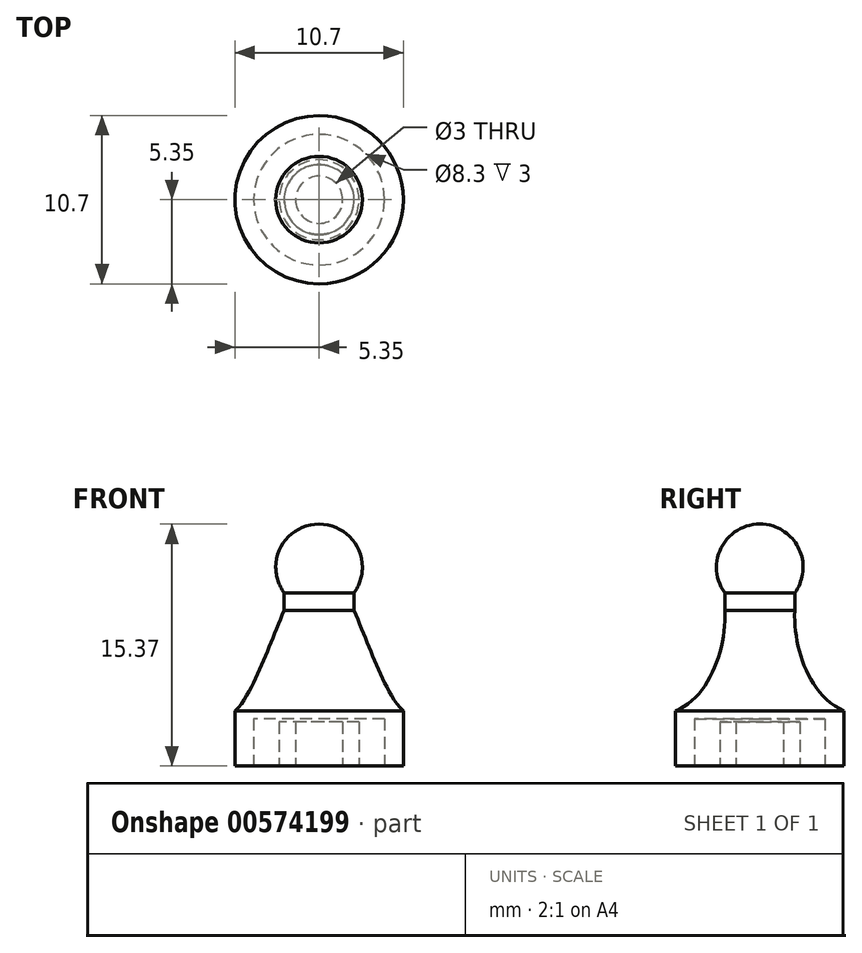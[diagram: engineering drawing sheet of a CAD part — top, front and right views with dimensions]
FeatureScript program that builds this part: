
annotation { "Feature Type Name" : "Feature", "Feature Type Description" : "" }
export const myFeature = defineFeature(function(context is Context, id is Id, definition is map)
    precondition{}
    {
        {
            var Q0;
            Q0=qCreatedBy(makeId("Top.planeOp"),FACE);
            var sketch = newSketch(context, id + "F0", { "sketchPlane" : qUnion([Q0])});
            skCircle(sketch, "E0", {"center": v(0, 0) * mm, "radius": 5.34 * mm});
            skPoint(sketch, "E1", {"position": v(0, -5.34) * mm});
            skSolve(sketch);
        }
        {
            var Q0;
            Q0=qCreatedBy(makeId("Top.planeOp"),FACE);
            cPlane(context, id + "F1", {"entities" : qUnion([Q0]), "cplaneType" : CPlaneType.OFFSET, "offset" : 9.87 * mm, "width" : 150 * mm, "height" : 150 * mm});
        }
        {
            var Q0;
            Q0=qCreatedBy(id+"F1.planeOp",FACE);
            var sketch = newSketch(context, id + "F2", { "sketchPlane" : qUnion([Q0])});
            skPoint(sketch, "E2", {"position": v(0, 0) * mm});
            skCircle(sketch, "E3", {"center": v(0, 0) * mm, "radius": 2.22 * mm});
            skPoint(sketch, "E4", {"position": v(0, -2.22) * mm});
            skSolve(sketch);
        }
        {
            var Q0;
            Q0=makeQuery(id+"F0.imprint","IMPRINT",FACE,{"disambiguationData":[TD([[makeQuery(id+"F0.imprint","IMPRINT",EDGE,{"derivedFrom":sQuery(id+"F0.wireOp",EDGE,"E0")}),1.0]])]});
            extrude(context, id + "F3", {"entities" : qUnion([Q0]), "depth" : 3.5 * mm, "offsetDistance" : 25 * mm});
        }
        {
            var Q0;
            Q0=qCreatedBy(makeId("Right.planeOp"),FACE);
            var sketch = newSketch(context, id + "F4", { "sketchPlane" : qUnion([Q0])});
            skPoint(sketch, "E5", {"position": v(-5.34, 3.5) * mm});
            skFitSpline(sketch, "E6", {"points": [v(-5.34, 3.5) * mm, v(-2.22, 9.87) * mm], "startDerivative": vector(6.48, 2.72) * mm, "endDerivative": vector(-0.3, 7.3) * mm});
            skLineSegment(sketch, "E7", {"start": v(0, 10.7) * mm, "end": v(0, 0) * mm, "construction": true});
            skFitSpline(sketch, "E8.MirrorCS", {"points": [v(5.35, 3.5) * mm, v(2.22, 9.87) * mm], "startDerivative": vector(-6.48, 2.72) * mm, "endDerivative": vector(0.3, 7.3) * mm});
            skSolve(sketch);
        }
        {
            var Q1;
            Q1=makeQuery(id+"F3.opExtrude","CAP_FACE",FACE,{"disambiguationData":[OSD([sQuery(id+"F0.wireOp",EDGE,"E0")])],"isStart":false});
            var Q2;
            Q2=makeQuery(id+"F2.imprint","IMPRINT",FACE,{"disambiguationData":[TD([[makeQuery(id+"F2.imprint","IMPRINT",EDGE,{"derivedFrom":sQuery(id+"F2.wireOp",EDGE,"E3")}),1.0]])]});
            var Q3;
            Q3=sQuery(id+"F4.wireOp",EDGE,"E6");
            var Q4;
            Q4=sQuery(id+"F4.wireOp",EDGE,"E8.MirrorCS");
            loft(context, id + "F5", {"operationType" : NewBodyOperationType.ADD, "addGuides" : true, "sheetProfilesArray" : [{ "sheetProfileEntities" : qUnion([Q1]) }, { "sheetProfileEntities" : qUnion([Q2]) }], "guidesArray" : [{ "guideEntities" : qUnion([Q3]), "guideDerivativeType" : LoftGuideDerivativeType.DEFAULT, "guideDerivativeMagnitude" : 1 }, { "guideEntities" : qUnion([Q4]), "guideDerivativeType" : LoftGuideDerivativeType.DEFAULT, "guideDerivativeMagnitude" : 1 }]});
        }
        {
            var Q0;
            Q0=qCreatedBy(id+"F1.planeOp",FACE);
            cPlane(context, id + "F6", {"entities" : qUnion([Q0]), "cplaneType" : CPlaneType.OFFSET, "offset" : (5.5 / 2) * mm, "width" : 150 * mm, "height" : 150 * mm});
        }
        {
            var Q0;
            Q0=qCreatedBy(id+"F6.planeOp",FACE);
            var sketch = newSketch(context, id + "F7", { "sketchPlane" : qUnion([Q0])});
            skPoint(sketch, "E9", {"position": v(0, 0) * mm});
            skArc(sketch, "E10", {"start": v(2.75, 0) * mm, "mid": v(0, 2.75) * mm, "end": v(-2.75, 0) * mm});
            skLineSegment(sketch, "E11", {"start": v(7.18, 0) * mm, "end": v(-9.15, 0) * mm, "construction": true});
            skLineSegment(sketch, "E12", {"start": v(-2.75, 0) * mm, "end": v(2.75, 0) * mm});
            skSolve(sketch);
        }
        {
            var Q0;
            Q0=makeQuery(id+"F7.imprint","IMPRINT",FACE,{"disambiguationData":[TD([[makeQuery(id+"F7.imprint","IMPRINT",EDGE,{"derivedFrom":sQuery(id+"F7.wireOp",EDGE,"E10")}),1.0]])]});
            var Q1;
            Q1=sQuery(id+"F7.wireOp",EDGE,"E11");
            revolve(context, id + "F8", {"entities" : qUnion([Q0]), "axis" : qUnion([Q1]), "revolveType" : RevolveType.FULL});
        }
        {
            var Q0;
            Q0=makeQuery(id+"F2.imprint","IMPRINT",FACE,{"disambiguationData":[TD([[makeQuery(id+"F2.imprint","IMPRINT",EDGE,{"derivedFrom":sQuery(id+"F2.wireOp",EDGE,"E3")}),1.0]])]});
            extrude(context, id + "F9", {"entities" : qUnion([Q0]), "operationType" : NewBodyOperationType.ADD, "endBound" : BoundingType.UP_TO_NEXT, "depth" : 25 * mm, "offsetDistance" : 25 * mm});
        }
        {
            var Q0;
            Q0=qCreatedBy(makeId("Top.planeOp"),FACE);
            var sketch = newSketch(context, id + "F10", { "sketchPlane" : qUnion([Q0])});
            skCircle(sketch, "E13", {"center": v(0, 0) * mm, "radius": 4.15 * mm});
            skSolve(sketch);
        }
        {
            var Q0;
            Q0=qSketchRegion(id+"F10",true);
            extrude(context, id + "F11", {"entities" : qUnion([Q0]), "operationType" : NewBodyOperationType.REMOVE, "depth" : 3 * mm, "offsetDistance" : 25 * mm});
        }
        {
            var Q0;
            Q0=qCreatedBy(makeId("Top.planeOp"),FACE);
            var sketch = newSketch(context, id + "F12", { "sketchPlane" : qUnion([Q0])});
            skCircle(sketch, "E14", {"center": v(0, 0) * mm, "radius": 2.54 * mm});
            skSolve(sketch);
        }
        {
            var Q0;
            Q0=qSketchRegion(id+"F12",true);
            extrude(context, id + "F13", {"entities" : qUnion([Q0]), "depth" : 2.8 * mm, "offsetDistance" : 25 * mm});
        }
        {
            var Q0;
            Q0=makeQuery(id+"F13.opExtrude","CAP_FACE",FACE,{"disambiguationData":[OSD([sQuery(id+"F12.wireOp",EDGE,"E14")])],"isStart":true});
            var sketch = newSketch(context, id + "F14", { "sketchPlane" : qUnion([Q0])});
            skCircle(sketch, "E15", {"center": v(0, 0) * mm, "radius": 1.5 * mm});
            skSolve(sketch);
        }
        {
            var Q0;
            Q0=qSketchRegion(id+"F14",true);
            extrude(context, id + "F15", {"entities" : qUnion([Q0]), "operationType" : NewBodyOperationType.REMOVE, "oppositeDirection" : true, "depth" : 2.9 * mm, "offsetDistance" : 25 * mm});
        }
    });
